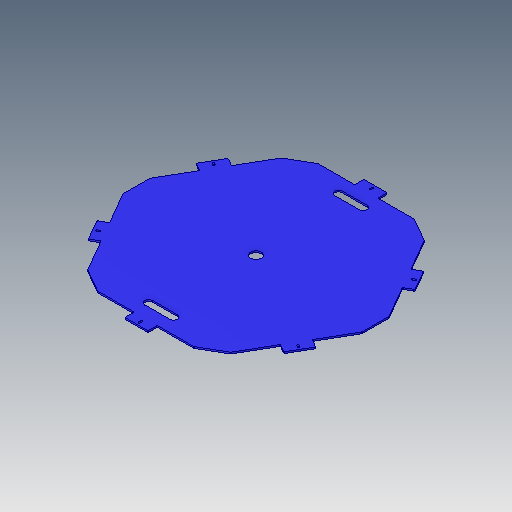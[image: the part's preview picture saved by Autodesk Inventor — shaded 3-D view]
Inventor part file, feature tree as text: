
AUTODESK INVENTOR PART (.ipt)
format: ipt  version: 2023.5 (Build 275446000, 446)  size: 167,936 bytes
history: native  units: in
note: dims shown in document units (in); Inventor stores cm internally (conversion verified against a paired STEP export)
features: fillet x1
ambient origin geometry x8: Origin, YZ Plane, XZ Plane, XY Plane, X Axis, Y Axis, Z Axis, Center Point
bodies: Solid1 (feature_tree)
feature tree (1):
  fillet  "Fillet2"  [1 undecoded]
note: 1 required parameter value undecoded (feature->parameter linkage not recoverable at this tier; creation-order binding heuristic only, values carry confidence <= 0.55)
